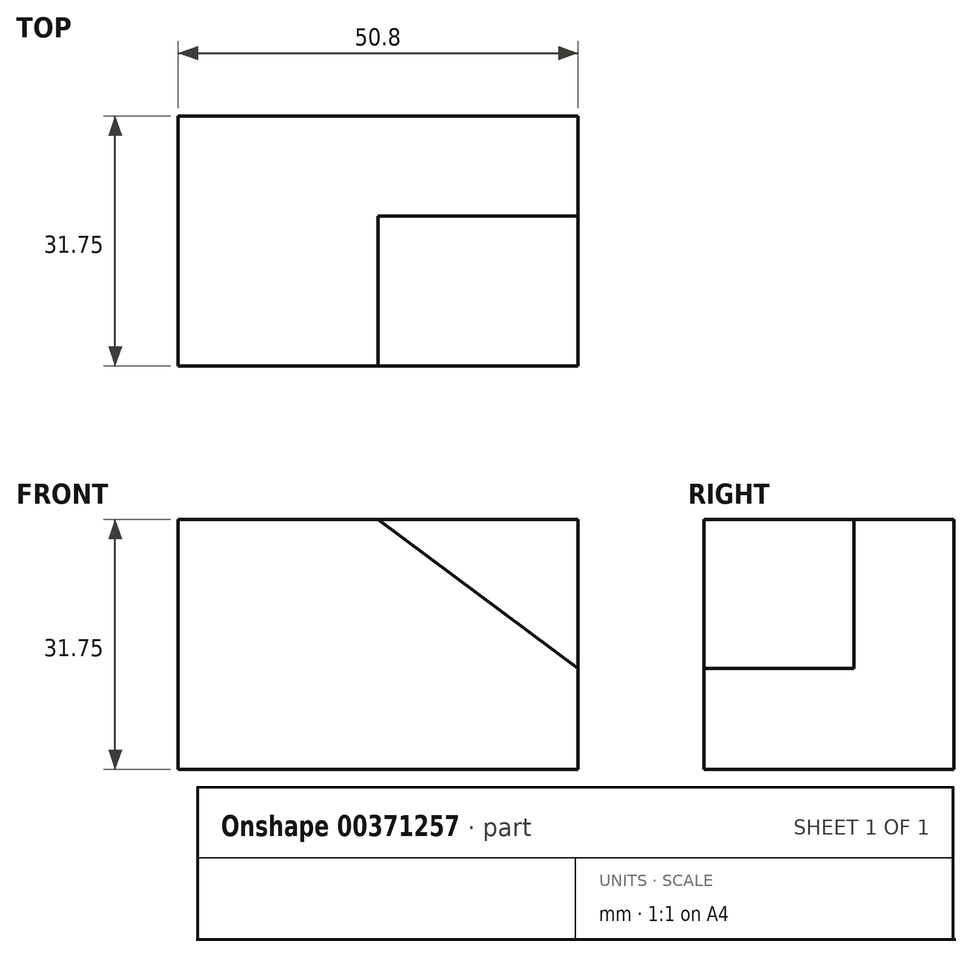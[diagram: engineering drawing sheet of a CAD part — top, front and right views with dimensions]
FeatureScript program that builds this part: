
annotation { "Feature Type Name" : "Feature", "Feature Type Description" : "" }
export const myFeature = defineFeature(function(context is Context, id is Id, definition is map)
    precondition{}
    {
        {
            var Q0;
            Q0=qCreatedBy(makeId("Front.planeOp"),FACE);
            var sketch = newSketch(context, id + "F0", { "sketchPlane" : qUnion([Q0])});
            skLineSegment(sketch, "E0", {"start": v(0, 31.75) * mm, "end": v(0, 0) * mm});
            skLineSegment(sketch, "E1", {"start": v(0, 0) * mm, "end": v(50.8, 0) * mm});
            skLineSegment(sketch, "E2", {"start": v(50.8, 0) * mm, "end": v(50.8, 31.75) * mm});
            skLineSegment(sketch, "E3", {"start": v(50.8, 31.75) * mm, "end": v(0, 31.75) * mm});
            skSolve(sketch);
        }
        {
            var Q0;
            Q0=makeQuery(id+"F0.imprint","IMPRINT",FACE,{"disambiguationData":[TD([[makeQuery(id+"F0.imprint","IMPRINT",EDGE,{"derivedFrom":sQuery(id+"F0.wireOp",EDGE,"E0")}),1.0]])]});
            extrude(context, id + "F1", {"entities" : qUnion([Q0]), "depth" : 31.75 * mm});
        }
        {
            var Q0;
            Q0=makeQuery(id+"F1.opExtrude","CAP_FACE",FACE,{"disambiguationData":[OSD([sQuery(id+"F0.wireOp",EDGE,"E0"),sQuery(id+"F0.wireOp",EDGE,"E1"),sQuery(id+"F0.wireOp",EDGE,"E2"),sQuery(id+"F0.wireOp",EDGE,"E3")])],"isStart":false});
            var sketch = newSketch(context, id + "F2", { "sketchPlane" : qUnion([Q0])});
            skLineSegment(sketch, "E4", {"start": v(25.4, 31.75) * mm, "end": v(50.8, 12.84) * mm});
            skSolve(sketch);
        }
        {
            var Q0;
            {var subQ0=sQuery(id+"F2.wireOp",EDGE,"E4");Q0=makeQuery(id+"F2.imprint","IMPRINT",FACE,{"disambiguationData":[TD([[makeQuery(id+"F2.imprint","IMPRINT",EDGE,{"derivedFrom":subQ0}),1.0]])]});}
            extrude(context, id + "F3", {"entities" : qUnion([Q0]), "operationType" : NewBodyOperationType.REMOVE, "oppositeDirection" : true, "depth" : 19.05 * mm});
        }
    });
